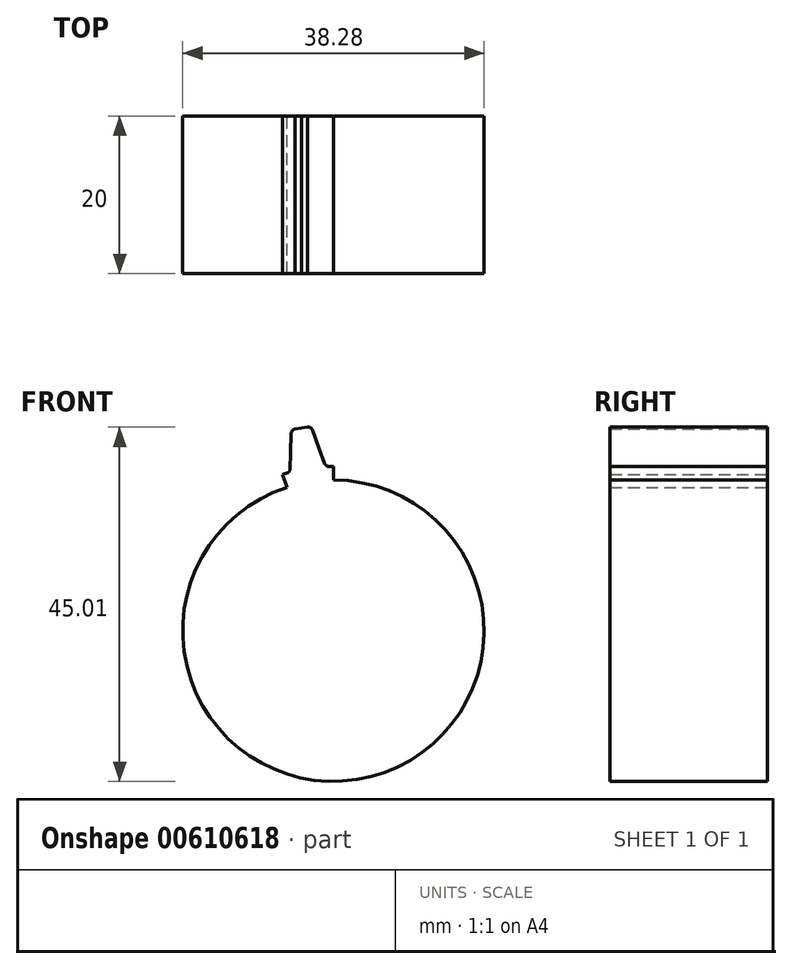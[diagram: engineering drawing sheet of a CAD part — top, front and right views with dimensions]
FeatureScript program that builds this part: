
annotation { "Feature Type Name" : "Feature", "Feature Type Description" : "" }
export const myFeature = defineFeature(function(context is Context, id is Id, definition is map)
    precondition{}
    {
        {
            var Q0;
            Q0=qCreatedBy(makeId("Front.planeOp"),FACE);
            var sketch = newSketch(context, id + "F0", { "sketchPlane" : qUnion([Q0])});
            skLineSegment(sketch, "E0", {"start": v(-5.92, 18.2) * mm, "end": v(-6.45, 19.84) * mm});
            skLineSegment(sketch, "E1", {"start": v(-3, 18.9) * mm, "end": v(-4.08, 25.75) * mm});
            skLineSegment(sketch, "E2", {"start": v(-5.51, 20.55) * mm, "end": v(-5.44, 22.58) * mm});
            skArc(sketch, "E3", {"start": v(-4.88, 25.61) * mm, "mid": v(-5.21, 25.42) * mm, "end": v(-5.36, 25.05) * mm});
            skLineSegment(sketch, "E4", {"start": v(-5.36, 25.05) * mm, "end": v(-5.44, 22.58) * mm});
            skLineSegment(sketch, "E5", {"start": v(-4.88, 25.61) * mm, "end": v(-4.08, 25.75) * mm});
            skLineSegment(sketch, "E6.MirrorCS", {"start": v(-3.28, 25.87) * mm, "end": v(-4.08, 25.75) * mm});
            skArc(sketch, "E7.MirrorCS", {"start": v(-3.28, 25.87) * mm, "mid": v(-2.9, 25.78) * mm, "end": v(-2.65, 25.48) * mm});
            skLineSegment(sketch, "E8.MirrorCS", {"start": v(-2.65, 25.48) * mm, "end": v(-1.8, 23.16) * mm});
            skLineSegment(sketch, "E9.MirrorCS", {"start": v(-1.1, 21.25) * mm, "end": v(-1.8, 23.16) * mm});
            skArc(sketch, "E10.trimOffspring", {"start": v(-5.92, 20) * mm, "mid": v(-5.63, 20.22) * mm, "end": v(-5.51, 20.55) * mm});
            skPoint(sketch, "E11.MirrorCS.end.orphan", {"position": v(-1.1, 21.25) * mm});
            skArc(sketch, "E12.MirrorCS", {"start": v(-0.55, 20.86) * mm, "mid": v(-0.89, 20.97) * mm, "end": v(-1.1, 21.25) * mm});
            skLineSegment(sketch, "E13", {"start": v(-6.45, 19.84) * mm, "end": v(-5.92, 20) * mm});
            skLineSegment(sketch, "E14.MirrorCS", {"start": v(0, 20.86) * mm, "end": v(-0.55, 20.86) * mm});
            skLineSegment(sketch, "E15", {"start": v(0, 20.86) * mm, "end": v(0, 19.14) * mm});
            skCircle(sketch, "E16", {"center": v(0, 0) * mm, "radius": 19.14 * mm});
            skSolve(sketch);
        }
        {
            var Q0;
            {var subQ0=sQuery(id+"F0.wireOp",EDGE,"E16");var subQ1=makeQuery(id+"F0.imprint","INTERSECT",VERTEX,{"derivedFrom":[sQuery(id+"F0.wireOp",EDGE,"E1"),subQ0]});Q0=makeQuery(id+"F0.imprint","IMPRINT",FACE,{"disambiguationData":[TD([[makeQuery(id+"F0.imprint","IMPRINT",EDGE,{"disambiguationData":[TD([[subQ1,1.0]])],"derivedFrom":subQ0}),1.0]])]});}
            var Q1;
            {var subQ1=sQuery(id+"F0.wireOp",EDGE,"E0");Q1=makeQuery(id+"F0.imprint","IMPRINT",FACE,{"disambiguationData":[TD([[makeQuery(id+"F0.imprint","IMPRINT",EDGE,{"derivedFrom":subQ1}),-1.0]])]});}
            var Q2;
            {var subQ0=sQuery(id+"F0.wireOp",EDGE,"E1");Q2=makeQuery(id+"F0.imprint","IMPRINT",FACE,{"disambiguationData":[TD([[makeQuery(id+"F0.imprint","IMPRINT",EDGE,{"derivedFrom":subQ0}),-1.0]])]});}
            extrude(context, id + "F1", {"entities" : qUnion([Q0, Q1, Q2]), "depth" : 20 * mm, "offsetDistance" : 25 * mm});
        }
    });
